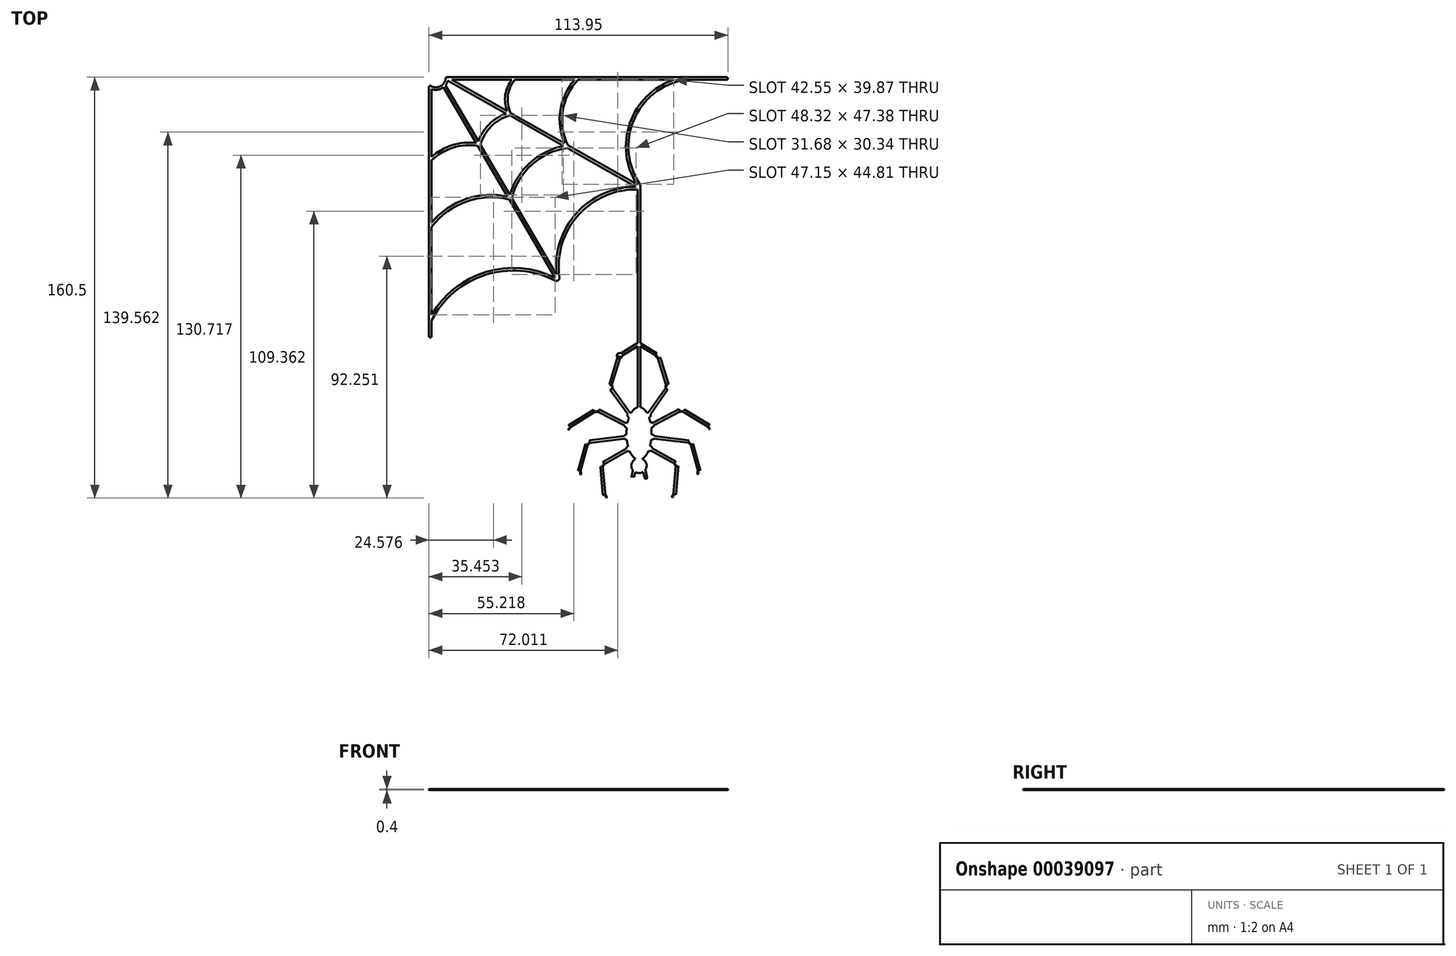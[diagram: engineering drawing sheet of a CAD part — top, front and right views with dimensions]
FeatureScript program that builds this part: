
annotation { "Feature Type Name" : "Feature", "Feature Type Description" : "" }
export const myFeature = defineFeature(function(context is Context, id is Id, definition is map)
    precondition{}
    {
        {
            var Q0;
            Q0=qCreatedBy(makeId("Top.planeOp"),FACE);
            var sketch = newSketch(context, id + "F0", { "sketchPlane" : qUnion([Q0])});
            skPoint(sketch, "E0.endSnap0", {"position": v(-98.37, 53.24) * mm});
            skLineSegment(sketch, "E1.5.startCap", {"start": v(-10.38, 79.69) * mm, "end": v(-10.38, 79.69) * mm});
            skArc(sketch, "E1.5.left", {"start": v(-10.2, 78.7) * mm, "mid": v(-29.48, 63.21) * mm, "end": v(-26.9, 38.61) * mm});
            skArc(sketch, "E1.5.right", {"start": v(-14.23, 78.7) * mm, "mid": v(-30.95, 62.17) * mm, "end": v(-28.25, 38.83) * mm});
            skArc(sketch, "E1.6.startCap", {"start": v(-101.16, 79.24) * mm, "mid": v(-101, 79.57) * mm, "end": v(-100.66, 79.7) * mm});
            skArc(sketch, "E1.6.endCap", {"start": v(5.93, 79.7) * mm, "mid": v(6.43, 79.2) * mm, "end": v(5.93, 78.7) * mm});
            skLineSegment(sketch, "E1.6.left", {"start": v(-100.66, 79.7) * mm, "end": v(5.93, 79.7) * mm});
            skArc(sketch, "E1.7.startCap", {"start": v(-101.16, 79.24) * mm, "mid": v(-101, 79.57) * mm, "end": v(-100.66, 79.7) * mm});
            skLineSegment(sketch, "E1.7.left", {"start": v(-98.76, 78.7) * mm, "end": v(-77.67, 66.77) * mm});
            skLineSegment(sketch, "E1.7.right", {"start": v(-100.3, 78.41) * mm, "end": v(-78.03, 65.83) * mm});
            skLineSegment(sketch, "E1.8.left", {"start": v(-101.22, 76.58) * mm, "end": v(-88.68, 55.2) * mm});
            skLineSegment(sketch, "E1.8.right", {"start": v(-101.96, 75.86) * mm, "end": v(-89.5, 54.6) * mm});
            skArc(sketch, "E1.9.startCap", {"start": v(-107.52, 75.91) * mm, "mid": v(-107.27, 76.35) * mm, "end": v(-106.77, 76.35) * mm});
            skArc(sketch, "E1.9.endCap", {"start": v(-106.52, -19.05) * mm, "mid": v(-107.02, -19.55) * mm, "end": v(-107.52, -19.05) * mm});
            skLineSegment(sketch, "E1.9.left", {"start": v(-106.52, 75.13) * mm, "end": v(-106.52, 49.32) * mm});
            skLineSegment(sketch, "E1.9.right", {"start": v(-107.52, 75.91) * mm, "end": v(-107.52, -19.05) * mm});
            skArc(sketch, "E1.10.startCap", {"start": v(-75.03, 79.7) * mm, "mid": v(-75.03, 79.7) * mm, "end": v(-75.02, 79.7) * mm});
            skArc(sketch, "E1.10.left", {"start": v(-74.65, 78.87) * mm, "mid": v(-77.4, 72.71) * mm, "end": v(-76.38, 66.04) * mm});
            skArc(sketch, "E1.15.startCap", {"start": v(-76.4, 33.94) * mm, "mid": v(-76.22, 33.86) * mm, "end": v(-76.1, 33.71) * mm});
            skArc(sketch, "E1.15.endCap", {"start": v(-107.52, 22.78) * mm, "mid": v(-107.5, 22.94) * mm, "end": v(-107.42, 23.08) * mm});
            skArc(sketch, "E1.15.left", {"start": v(-76.65, 32.97) * mm, "mid": v(-93.23, 32.29) * mm, "end": v(-106.62, 22.48) * mm});
            skArc(sketch, "E1.20.right", {"start": v(-28.61, 37.89) * mm, "mid": v(-51.23, 27.9) * mm, "end": v(-58.92, 4.4) * mm});
            skLineSegment(sketch, "E1.22.endCap", {"start": v(-106.57, -13.15) * mm, "end": v(-106.57, -13.15) * mm});
            skArc(sketch, "E1.22.left", {"start": v(-59.5, 2.14) * mm, "mid": v(-86.21, 4.27) * mm, "end": v(-106.57, -13.15) * mm});
            skArc(sketch, "E1.22.right", {"start": v(-59.37, 3.2) * mm, "mid": v(-85.75, 5.46) * mm, "end": v(-106.52, -10.96) * mm});
            skArc(sketch, "E1.23.startCap", {"start": v(-50.82, 79.7) * mm, "mid": v(-50.81, 79.7) * mm, "end": v(-50.8, 79.7) * mm});
            skArc(sketch, "E1.23.left", {"start": v(-50.46, 78.84) * mm, "mid": v(-56.52, 66.83) * mm, "end": v(-54.42, 53.53) * mm});
            skArc(sketch, "E1.23.right", {"start": v(-51.96, 78.7) * mm, "mid": v(-57.44, 67.14) * mm, "end": v(-55.86, 54.44) * mm});
            skArc(sketch, "E1.28.left", {"start": v(-76.53, 65.14) * mm, "mid": v(-83.77, 61) * mm, "end": v(-87.94, 53.76) * mm});
            skArc(sketch, "E1.31.left", {"start": v(-88.62, 53.46) * mm, "mid": v(-98.33, 52.83) * mm, "end": v(-106.67, 47.81) * mm});
            skArc(sketch, "E1.31.right", {"start": v(-89.5, 54.6) * mm, "mid": v(-98.58, 53.8) * mm, "end": v(-106.52, 49.32) * mm});
            skArc(sketch, "E1.36.startCap", {"start": v(-54.83, 53.74) * mm, "mid": v(-54.66, 53.73) * mm, "end": v(-54.5, 53.68) * mm});
            skLineSegment(sketch, "E1.36.endCap", {"start": v(-76.04, 33.34) * mm, "end": v(-76.04, 33.34) * mm});
            skArc(sketch, "E1.36.left", {"start": v(-54.81, 52.73) * mm, "mid": v(-68.39, 46.28) * mm, "end": v(-76.04, 33.34) * mm});
            skArc(sketch, "E1.36.right", {"start": v(-56.23, 53.5) * mm, "mid": v(-69.1, 47) * mm, "end": v(-76.7, 34.75) * mm});
            skArc(sketch, "E1.38.startCap", {"start": v(-107.52, 75.91) * mm, "mid": v(-107.27, 76.35) * mm, "end": v(-106.77, 76.35) * mm});
            skArc(sketch, "E1.38.endCap", {"start": v(-101.16, 79.24) * mm, "mid": v(-101, 79.57) * mm, "end": v(-100.66, 79.7) * mm});
            skArc(sketch, "E1.38.left", {"start": v(-106.77, 76.35) * mm, "mid": v(-103.17, 76.26) * mm, "end": v(-101.16, 79.24) * mm});
            skArc(sketch, "E1.38.right", {"start": v(-106.52, 75.13) * mm, "mid": v(-104.14, 74.9) * mm, "end": v(-101.96, 75.86) * mm});
            skLineSegment(sketch, "E2.trimOffspring", {"start": v(-106.52, -13.05) * mm, "end": v(-106.52, -19.05) * mm});
            skArc(sketch, "E3.trimOffspring", {"start": v(-107.52, -12.93) * mm, "mid": v(-107.5, -12.8) * mm, "end": v(-107.46, -12.7) * mm});
            skLineSegment(sketch, "E4.trimOffspring", {"start": v(-106.52, 22.62) * mm, "end": v(-106.52, -10.96) * mm});
            skLineSegment(sketch, "E5.trimOffspring", {"start": v(-76.1, 33.71) * mm, "end": v(-58.92, 4.4) * mm});
            skLineSegment(sketch, "E6.trimOffspring", {"start": v(-76.96, 33.2) * mm, "end": v(-59.37, 3.2) * mm});
            skArc(sketch, "E7.trimOffspring", {"start": v(-77.55, 34.22) * mm, "mid": v(-93.43, 33.27) * mm, "end": v(-106.52, 24.22) * mm});
            skLineSegment(sketch, "E8.trimOffspring", {"start": v(-106.52, 47.96) * mm, "end": v(-106.52, 24.22) * mm});
            skLineSegment(sketch, "E9.trimOffspring", {"start": v(-88.1, 54.2) * mm, "end": v(-76.7, 34.75) * mm});
            skLineSegment(sketch, "E10.trimOffspring", {"start": v(-88.85, 53.5) * mm, "end": v(-77.55, 34.22) * mm});
            skLineSegment(sketch, "E11.trimOffspring", {"start": v(-76.4, 66.06) * mm, "end": v(-55.86, 54.44) * mm});
            skArc(sketch, "E12.trimOffspring", {"start": v(-78.03, 65.83) * mm, "mid": v(-84.6, 61.75) * mm, "end": v(-88.68, 55.2) * mm});
            skLineSegment(sketch, "E13.trimOffspring", {"start": v(-76.72, 65.09) * mm, "end": v(-56.23, 53.5) * mm});
            skLineSegment(sketch, "E14.trimOffspring", {"start": v(-54.85, 52.72) * mm, "end": v(-28.61, 37.89) * mm});
            skLineSegment(sketch, "E15.trimOffspring", {"start": v(-54.49, 53.66) * mm, "end": v(-28.25, 38.83) * mm});
            skArc(sketch, "E16.trimOffspring", {"start": v(-55.11, 52.87) * mm, "mid": v(-55.23, 52.96) * mm, "end": v(-55.31, 53.08) * mm});
            skLineSegment(sketch, "E17.trimOffspring", {"start": v(-10.25, 78.7) * mm, "end": v(5.93, 78.7) * mm});
            skLineSegment(sketch, "E18.trimOffspring", {"start": v(-50.6, 78.7) * mm, "end": v(-14.23, 78.7) * mm});
            skLineSegment(sketch, "E19.trimOffspring", {"start": v(-74.8, 78.7) * mm, "end": v(-51.96, 78.7) * mm});
            skLineSegment(sketch, "E20.trimOffspring", {"start": v(-98.76, 78.7) * mm, "end": v(-75.94, 78.7) * mm});
            skArc(sketch, "E21.trimOffspring", {"start": v(-101.22, 76.58) * mm, "mid": v(-100.66, 77.45) * mm, "end": v(-100.3, 78.41) * mm});
            skArc(sketch, "E22", {"start": v(-75.94, 78.7) * mm, "mid": v(-78.42, 72.97) * mm, "end": v(-77.67, 66.77) * mm});
            skLineSegment(sketch, "E23.0.right", {"start": v(-22.6, -53.42) * mm, "end": v(-10.92, -47.39) * mm});
            skLineSegment(sketch, "E23.21.left", {"start": v(0.43, -53.66) * mm, "end": v(2.06, -65.33) * mm});
            skEllipse(sketch, "E24", {"center": v(-27.45, -68.45) * mm, "majorRadius": 2.83 * mm, "minorRadius": 2.91 * mm, "majorAxis": v(0, 1)});
            skEllipse(sketch, "E25", {"center": v(-27.45, -56.16) * mm, "majorRadius": 10.03 * mm, "minorRadius": 4.77 * mm, "majorAxis": v(0, 1)});
            skLineSegment(sketch, "E23.0.left", {"start": v(-23.06, -52.53) * mm, "end": v(-11.37, -46.5) * mm});
            skLineSegment(sketch, "E23.3.right", {"start": v(-34.63, -26.94) * mm, "end": v(-27.9, -22.81) * mm});
            skLineSegment(sketch, "E23.17.left", {"start": v(-3.76, -71.27) * mm, "end": v(-6.93, -83.23) * mm});
            skLineSegment(sketch, "E23.3.left", {"start": v(-35.15, -26.09) * mm, "end": v(-27.9, -21.64) * mm});
            skLineSegment(sketch, "E23.35.right", {"start": v(-23.62, -62.32) * mm, "end": v(-13.14, -68.15) * mm});
            skLineSegment(sketch, "E23.26.left", {"start": v(-43.43, -47.46) * mm, "end": v(-54.48, -54.32) * mm});
            skLineSegment(sketch, "E23.25.right", {"start": v(-23.53, -49.46) * mm, "end": v(-15.96, -38.67) * mm});
            skLineSegment(sketch, "E23.21.right", {"start": v(-0.56, -53.8) * mm, "end": v(1.07, -65.47) * mm});
            skLineSegment(sketch, "E23.13.left", {"start": v(-26.92, -11.26) * mm, "end": v(-26.9, -21.74) * mm});
            skLineSegment(sketch, "E23.17.right", {"start": v(-4.72, -71.01) * mm, "end": v(-7.9, -82.97) * mm});
            skLineSegment(sketch, "E23.25.left", {"start": v(-24.35, -48.88) * mm, "end": v(-16.78, -38.1) * mm});
            skLineSegment(sketch, "E23.8.endCap", {"start": v(-27.36, 17.93) * mm, "end": v(-27.36, 17.93) * mm});
            skLineSegment(sketch, "E23.34.right", {"start": v(-15.9, -38.24) * mm, "end": v(-19.6, -26.32) * mm});
            skLineSegment(sketch, "E23.12.left", {"start": v(-12.4, -67.75) * mm, "end": v(-13.36, -80.35) * mm});
            skLineSegment(sketch, "E23.16.right", {"start": v(-30.48, -48.9) * mm, "end": v(-38.12, -38.16) * mm});
            skLineSegment(sketch, "E23.34.left", {"start": v(-16.85, -38.53) * mm, "end": v(-20.55, -26.62) * mm});
            skLineSegment(sketch, "E23.16.left", {"start": v(-31.3, -49.48) * mm, "end": v(-38.93, -38.74) * mm});
            skLineSegment(sketch, "E23.29.right", {"start": v(-55.24, -53.82) * mm, "end": v(-56.8, -65.5) * mm});
            skLineSegment(sketch, "E23.29.left", {"start": v(-54.25, -53.96) * mm, "end": v(-55.8, -65.63) * mm});
            skLineSegment(sketch, "E23.24.right", {"start": v(-41.1, -80.82) * mm, "end": v(-32.4, -90.55) * mm});
            skLineSegment(sketch, "E23.11.right", {"start": v(-38.05, -38.6) * mm, "end": v(-34.41, -26.66) * mm});
            skLineSegment(sketch, "E23.19.right", {"start": v(-42.27, -67.95) * mm, "end": v(-41.23, -80.53) * mm});
            skLineSegment(sketch, "E23.33.right", {"start": v(-11.4, -47.37) * mm, "end": v(-0.32, -54.16) * mm});
            skLineSegment(sketch, "E23.24.left", {"start": v(-40.24, -80.28) * mm, "end": v(-31.66, -89.89) * mm});
            skLineSegment(sketch, "E23.11.left", {"start": v(-39, -38.3) * mm, "end": v(-35.37, -26.37) * mm});
            skLineSegment(sketch, "E23.37.right", {"start": v(-47.7, -59.34) * mm, "end": v(-50.94, -71.15) * mm});
            skLineSegment(sketch, "E23.1.right", {"start": v(-19.81, -26.04) * mm, "end": v(-26.9, -21.74) * mm});
            skLineSegment(sketch, "E23.19.left", {"start": v(-41.27, -67.86) * mm, "end": v(-40.24, -80.28) * mm});
            skLineSegment(sketch, "E23.33.left", {"start": v(-10.88, -46.51) * mm, "end": v(0.2, -53.3) * mm});
            skLineSegment(sketch, "E23.30.right", {"start": v(-22.67, -58.03) * mm, "end": v(-7.61, -59.85) * mm});
            skLineSegment(sketch, "E23.37.left", {"start": v(-46.73, -59.6) * mm, "end": v(-49.98, -71.4) * mm});
            skLineSegment(sketch, "E23.27.right", {"start": v(-50.94, -71.4) * mm, "end": v(-47.7, -83.35) * mm});
            skLineSegment(sketch, "E23.1.left", {"start": v(-20.33, -26.9) * mm, "end": v(-26.9, -22.91) * mm});
            skLineSegment(sketch, "E23.14.right", {"start": v(-32.24, -57.07) * mm, "end": v(-47.28, -58.97) * mm});
            skLineSegment(sketch, "E23.27.left", {"start": v(-49.98, -71.15) * mm, "end": v(-46.73, -83.08) * mm});
            skLineSegment(sketch, "E23.32.right", {"start": v(-14.35, -80.1) * mm, "end": v(-22.87, -89.76) * mm});
            skLineSegment(sketch, "E23.14.left", {"start": v(-32.11, -58.06) * mm, "end": v(-47.15, -59.97) * mm});
            skLineSegment(sketch, "E23.18.right", {"start": v(-31.75, -52.56) * mm, "end": v(-43.47, -46.6) * mm});
            skLineSegment(sketch, "E23.32.left", {"start": v(-13.49, -80.64) * mm, "end": v(-22.12, -90.42) * mm});
            skLineSegment(sketch, "E23.18.left", {"start": v(-32.2, -53.45) * mm, "end": v(-43.93, -47.48) * mm});
            skLineSegment(sketch, "E23.4.right", {"start": v(-8.04, -59.49) * mm, "end": v(-4.72, -71.28) * mm});
            skLineSegment(sketch, "E23.4.left", {"start": v(-7.07, -59.22) * mm, "end": v(-3.76, -71) * mm});
            skLineSegment(sketch, "E23.12.right", {"start": v(-13.4, -67.68) * mm, "end": v(-14.35, -80.1) * mm});
            skLineSegment(sketch, "E23.26.right", {"start": v(-43.96, -46.61) * mm, "end": v(-55, -53.47) * mm});
            skCircle(sketch, "E26", {"center": v(-31.33, -62.01) * mm, "radius": 1 * mm});
            skArc(sketch, "E23.0.startCap", {"start": v(-22.6, -53.42) * mm, "mid": v(-22.72, -53.47) * mm, "end": v(-22.86, -53.48) * mm});
            skArc(sketch, "E23.21.endCap", {"start": v(2.06, -65.33) * mm, "mid": v(1.63, -65.9) * mm, "end": v(1.07, -65.47) * mm});
            skCircle(sketch, "E27", {"center": v(-22.83, -52.98) * mm, "radius": 1 * mm});
            skArc(sketch, "E23.39.startCap", {"start": v(-29.8, -70.51) * mm, "mid": v(-29.2, -70.14) * mm, "end": v(-28.83, -70.75) * mm});
            skArc(sketch, "E23.42.endCap", {"start": v(-25.3, -74.86) * mm, "mid": v(-25.98, -75.06) * mm, "end": v(-26.17, -74.38) * mm});
            skArc(sketch, "E23.29.endCap", {"start": v(-55.8, -65.63) * mm, "mid": v(-56.37, -66.06) * mm, "end": v(-56.8, -65.5) * mm});
            skArc(sketch, "E23.24.endCap", {"start": v(-31.66, -89.89) * mm, "mid": v(-31.7, -90.6) * mm, "end": v(-32.4, -90.55) * mm});
            skArc(sketch, "E23.17.endCap", {"start": v(-6.93, -83.23) * mm, "mid": v(-7.54, -83.58) * mm, "end": v(-7.9, -82.97) * mm});
            skArc(sketch, "E23.41.startCap", {"start": v(-25.88, -70.74) * mm, "mid": v(-25.52, -70.13) * mm, "end": v(-24.9, -70.5) * mm});
            skArc(sketch, "E23.27.endCap", {"start": v(-46.73, -83.08) * mm, "mid": v(-47.09, -83.7) * mm, "end": v(-47.7, -83.35) * mm});
            skArc(sketch, "E23.32.endCap", {"start": v(-22.12, -90.42) * mm, "mid": v(-22.83, -90.46) * mm, "end": v(-22.87, -89.76) * mm});
            skArc(sketch, "E23.14.startCap", {"start": v(-32.24, -57.07) * mm, "mid": v(-32.22, -57.06) * mm, "end": v(-32.2, -57.06) * mm});
            skCircle(sketch, "E28", {"center": v(-32.18, -57.56) * mm, "radius": 1 * mm});
            skArc(sketch, "E23.40.endCap", {"start": v(-28.51, -74.38) * mm, "mid": v(-28.7, -75.07) * mm, "end": v(-29.39, -74.88) * mm});
            skArc(sketch, "E23.13.endCap", {"start": v(-26.88, -58.8) * mm, "mid": v(-27.38, -59.3) * mm, "end": v(-27.88, -58.8) * mm});
            skArc(sketch, "E23.25.endCap", {"start": v(-15.9, -38.24) * mm, "mid": v(-15.88, -38.46) * mm, "end": v(-15.96, -38.67) * mm});
            skArc(sketch, "E23.25.startCap", {"start": v(-23.53, -49.46) * mm, "mid": v(-23.66, -49.58) * mm, "end": v(-23.82, -49.66) * mm});
            skArc(sketch, "E23.16.endCap", {"start": v(-38.93, -38.74) * mm, "mid": v(-39.02, -38.53) * mm, "end": v(-39, -38.3) * mm});
            skCircle(sketch, "E29", {"center": v(-31.98, -53) * mm, "radius": 1 * mm});
            skCircle(sketch, "E30", {"center": v(-23.37, -61.89) * mm, "radius": 1 * mm});
            skCircle(sketch, "E31", {"center": v(-38.52, -38.45) * mm, "radius": 1 * mm});
            skArc(sketch, "E23.18.startCap", {"start": v(-32.05, -53.5) * mm, "mid": v(-32.13, -53.48) * mm, "end": v(-32.2, -53.45) * mm});
            skCircle(sketch, "E32", {"center": v(-23.94, -49.17) * mm, "radius": 1 * mm});
            skCircle(sketch, "E33", {"center": v(-16.37, -38.39) * mm, "radius": 1 * mm});
            skCircle(sketch, "E34", {"center": v(-30.89, -49.2) * mm, "radius": 1 * mm});
            skArc(sketch, "E23.30.startCap", {"start": v(-22.67, -58.03) * mm, "mid": v(-22.72, -58.02) * mm, "end": v(-22.77, -58) * mm});
            skArc(sketch, "E23.12.endCap", {"start": v(-13.36, -80.35) * mm, "mid": v(-13.4, -80.5) * mm, "end": v(-13.49, -80.64) * mm});
            skArc(sketch, "E23.34.startCap", {"start": v(-15.9, -38.24) * mm, "mid": v(-15.88, -38.46) * mm, "end": v(-15.96, -38.67) * mm});
            skArc(sketch, "E23.16.startCap", {"start": v(-31.08, -49.65) * mm, "mid": v(-31.2, -49.58) * mm, "end": v(-31.3, -49.48) * mm});
            skCircle(sketch, "E35", {"center": v(-54.74, -53.9) * mm, "radius": 1 * mm});
            skArc(sketch, "E23.11.startCap", {"start": v(-38.93, -38.74) * mm, "mid": v(-39.02, -38.53) * mm, "end": v(-39, -38.3) * mm});
            skArc(sketch, "E23.19.endCap", {"start": v(-41.1, -80.82) * mm, "mid": v(-41.19, -80.69) * mm, "end": v(-41.23, -80.53) * mm});
            skCircle(sketch, "E36", {"center": v(-47.22, -59.47) * mm, "radius": 1 * mm});
            skArc(sketch, "E23.37.startCap", {"start": v(-47.7, -59.34) * mm, "mid": v(-47.54, -59.1) * mm, "end": v(-47.28, -58.97) * mm});
            skCircle(sketch, "E37", {"center": v(-40.73, -80.49) * mm, "radius": 1 * mm});
            skCircle(sketch, "E38", {"center": v(-22.6, -57.53) * mm, "radius": 1 * mm});
            skArc(sketch, "E23.35.startCap", {"start": v(-23.62, -62.32) * mm, "mid": v(-23.65, -62.3) * mm, "end": v(-23.68, -62.28) * mm});
            skCircle(sketch, "E39", {"center": v(-13.86, -80.3) * mm, "radius": 1 * mm});
            skLineSegment(sketch, "E23.39.right", {"start": v(-29.8, -70.51) * mm, "end": v(-30.37, -72.86) * mm});
            skArc(sketch, "E23.0.endCap", {"start": v(-11.37, -46.5) * mm, "mid": v(-11.13, -46.44) * mm, "end": v(-10.88, -46.51) * mm});
            skCircle(sketch, "E40", {"center": v(-50.46, -71.28) * mm, "radius": 1 * mm});
            skArc(sketch, "E23.40.startCap", {"start": v(-30.32, -73.22) * mm, "mid": v(-30.13, -72.54) * mm, "end": v(-29.45, -72.73) * mm});
            skCircle(sketch, "E41", {"center": v(-12.9, -67.72) * mm, "radius": 1 * mm});
            skLineSegment(sketch, "E23.42.right", {"start": v(-25.25, -72.72) * mm, "end": v(-26.17, -74.38) * mm});
            skCircle(sketch, "E42", {"center": v(-4.24, -71.14) * mm, "radius": 1 * mm});
            skLineSegment(sketch, "E23.42.left", {"start": v(-24.37, -73.2) * mm, "end": v(-25.3, -74.86) * mm});
            skArc(sketch, "E23.12.startCap", {"start": v(-12.65, -67.28) * mm, "mid": v(-12.46, -67.48) * mm, "end": v(-12.4, -67.75) * mm});
            skCircle(sketch, "E43", {"center": v(-0.06, -53.73) * mm, "radius": 1 * mm});
            skArc(sketch, "E23.42.startCap", {"start": v(-25.25, -72.72) * mm, "mid": v(-24.57, -72.52) * mm, "end": v(-24.37, -73.2) * mm});
            skCircle(sketch, "E44", {"center": v(-11.15, -46.94) * mm, "radius": 1 * mm});
            skLineSegment(sketch, "E23.41.right", {"start": v(-25.88, -70.74) * mm, "end": v(-25.3, -73.08) * mm});
            skArc(sketch, "E23.29.startCap", {"start": v(-55.24, -53.82) * mm, "mid": v(-55.16, -53.62) * mm, "end": v(-55, -53.47) * mm});
            skCircle(sketch, "E45", {"center": v(-43.7, -47.04) * mm, "radius": 1 * mm});
            skArc(sketch, "E23.33.endCap", {"start": v(0.2, -53.3) * mm, "mid": v(0.36, -53.46) * mm, "end": v(0.43, -53.66) * mm});
            skLineSegment(sketch, "E23.41.left", {"start": v(-24.9, -70.5) * mm, "end": v(-24.32, -72.84) * mm});
            skArc(sketch, "E23.24.startCap", {"start": v(-41.1, -80.82) * mm, "mid": v(-41.19, -80.69) * mm, "end": v(-41.23, -80.53) * mm});
            skArc(sketch, "E23.37.endCap", {"start": v(-50.94, -71.4) * mm, "mid": v(-50.96, -71.28) * mm, "end": v(-50.94, -71.15) * mm});
            skLineSegment(sketch, "E23.40.right", {"start": v(-30.32, -73.22) * mm, "end": v(-29.39, -74.88) * mm});
            skArc(sketch, "E23.14.endCap", {"start": v(-47.7, -59.34) * mm, "mid": v(-47.54, -59.1) * mm, "end": v(-47.28, -58.97) * mm});
            skLineSegment(sketch, "E23.39.left", {"start": v(-28.83, -70.75) * mm, "end": v(-29.4, -73.1) * mm});
            skLineSegment(sketch, "E23.40.left", {"start": v(-29.45, -72.73) * mm, "end": v(-28.51, -74.38) * mm});
            skArc(sketch, "E23.18.endCap", {"start": v(-43.96, -46.61) * mm, "mid": v(-43.72, -46.54) * mm, "end": v(-43.47, -46.6) * mm});
            skArc(sketch, "E23.32.startCap", {"start": v(-13.36, -80.35) * mm, "mid": v(-13.4, -80.5) * mm, "end": v(-13.49, -80.64) * mm});
            skArc(sketch, "E23.26.endCap", {"start": v(-55.24, -53.82) * mm, "mid": v(-55.16, -53.62) * mm, "end": v(-55, -53.47) * mm});
            skArc(sketch, "E23.39.endCap", {"start": v(-29.4, -73.1) * mm, "mid": v(-30, -73.46) * mm, "end": v(-30.37, -72.86) * mm});
            skArc(sketch, "E23.26.startCap", {"start": v(-43.96, -46.61) * mm, "mid": v(-43.72, -46.54) * mm, "end": v(-43.47, -46.6) * mm});
            skArc(sketch, "E23.41.endCap", {"start": v(-24.32, -72.84) * mm, "mid": v(-24.69, -73.45) * mm, "end": v(-25.3, -73.08) * mm});
            skArc(sketch, "E23.33.startCap", {"start": v(-11.37, -46.5) * mm, "mid": v(-11.13, -46.44) * mm, "end": v(-10.88, -46.51) * mm});
            skArc(sketch, "E23.35.endCap", {"start": v(-12.65, -67.28) * mm, "mid": v(-12.46, -67.48) * mm, "end": v(-12.4, -67.75) * mm});
            skArc(sketch, "E23.21.startCap", {"start": v(0.2, -53.3) * mm, "mid": v(0.36, -53.46) * mm, "end": v(0.43, -53.66) * mm});
            skArc(sketch, "E23.27.startCap", {"start": v(-50.94, -71.4) * mm, "mid": v(-50.96, -71.28) * mm, "end": v(-50.94, -71.15) * mm});
            skArc(sketch, "E23.4.endCap", {"start": v(-3.76, -71) * mm, "mid": v(-3.74, -71.14) * mm, "end": v(-3.76, -71.27) * mm});
            skArc(sketch, "E23.3.startCap", {"start": v(-34.63, -26.94) * mm, "mid": v(-35.32, -26.78) * mm, "end": v(-35.15, -26.09) * mm});
            skArc(sketch, "E23.17.startCap", {"start": v(-3.76, -71) * mm, "mid": v(-3.74, -71.14) * mm, "end": v(-3.76, -71.27) * mm});
            skCircle(sketch, "E46", {"center": v(-34.9, -26.51) * mm, "radius": 1 * mm});
            skArc(sketch, "E23.1.startCap", {"start": v(-19.81, -26.04) * mm, "mid": v(-19.68, -26.16) * mm, "end": v(-19.6, -26.32) * mm});
            skCircle(sketch, "E47", {"center": v(-20.07, -26.47) * mm, "radius": 1 * mm});
            skArc(sketch, "E23.30.endCap", {"start": v(-7.5, -58.86) * mm, "mid": v(-7.23, -58.97) * mm, "end": v(-7.07, -59.22) * mm});
            skCircle(sketch, "E48", {"center": v(-7.55, -59.35) * mm, "radius": 1 * mm});
            skArc(sketch, "E23.11.endCap", {"start": v(-35.37, -26.37) * mm, "mid": v(-35.29, -26.2) * mm, "end": v(-35.15, -26.09) * mm});
            skArc(sketch, "E23.2.endCap", {"start": v(-42.27, -67.95) * mm, "mid": v(-42.2, -67.67) * mm, "end": v(-42.01, -67.47) * mm});
            skCircle(sketch, "E49", {"center": v(-41.77, -67.9) * mm, "radius": 1 * mm});
            skArc(sketch, "E23.34.endCap", {"start": v(-19.81, -26.04) * mm, "mid": v(-19.68, -26.16) * mm, "end": v(-19.6, -26.32) * mm});
            skArc(sketch, "E23.4.startCap", {"start": v(-7.5, -58.86) * mm, "mid": v(-7.23, -58.97) * mm, "end": v(-7.07, -59.22) * mm});
            skArc(sketch, "E23.19.startCap", {"start": v(-42.27, -67.95) * mm, "mid": v(-42.2, -67.67) * mm, "end": v(-42.01, -67.47) * mm});
            skLineSegment(sketch, "E50.trimOffspring", {"start": v(-27.95, 36.88) * mm, "end": v(-27.9, -21.64) * mm});
            skArc(sketch, "E51.trimOffspring", {"start": v(-27.95, 36.88) * mm, "mid": v(-50.65, 27.05) * mm, "end": v(-57.78, 3.36) * mm});
            skLineSegment(sketch, "E52.trimOffspring", {"start": v(-27.9, -22.81) * mm, "end": v(-27.88, -58.8) * mm});
            skLineSegment(sketch, "E53.trimOffspring", {"start": v(-26.9, -22.91) * mm, "end": v(-26.88, -58.8) * mm});
            skArc(sketch, "E54", {"start": v(-59.5, 2.14) * mm, "mid": v(-58.26, 2.23) * mm, "end": v(-57.78, 3.36) * mm});
            skLineSegment(sketch, "E55", {"start": v(-26.92, -11.26) * mm, "end": v(-26.9, 38.61) * mm});
            skLineSegment(sketch, "E56.trimOffspring", {"start": v(-22.7, -57.02) * mm, "end": v(-7.5, -58.86) * mm});
            skLineSegment(sketch, "E57.trimOffspring", {"start": v(-23.37, -61.32) * mm, "end": v(-12.65, -67.28) * mm});
            skLineSegment(sketch, "E58.trimOffspring", {"start": v(-31.48, -61.53) * mm, "end": v(-42.01, -67.47) * mm});
            skLineSegment(sketch, "E59.trimOffspring", {"start": v(-31.15, -62.5) * mm, "end": v(-41.52, -68.34) * mm});
            skSolve(sketch);
        }
        {
            var Q0;
            {var subQ3=sQuery(id+"F0.wireOp",EDGE,"E23.26.left");var subQ5=sQuery(id+"F0.wireOp",EDGE,"E45");var subQ7=makeQuery(id+"F0.imprint","INTERSECT",VERTEX,{"derivedFrom":[subQ3,subQ5]});Q0=makeQuery(id+"F0.imprint","IMPRINT",FACE,{"disambiguationData":[TD([[makeQuery(id+"F0.imprint","IMPRINT",EDGE,{"disambiguationData":[TD([[subQ7,-1.0]])],"derivedFrom":subQ3}),-1.0]])]});}
            var Q1;
            {var subQ0=sQuery(id+"F0.wireOp",EDGE,"E49");var subQ3=sQuery(id+"F0.wireOp",EDGE,"E23.19.right");var subQ4=makeQuery(id+"F0.imprint","INTERSECT",VERTEX,{"derivedFrom":[subQ3,subQ0]});Q1=makeQuery(id+"F0.imprint","IMPRINT",FACE,{"disambiguationData":[TD([[makeQuery(id+"F0.imprint","IMPRINT",EDGE,{"disambiguationData":[TD([[subQ4,-1.0]])],"derivedFrom":subQ3}),1.0]])]});}
            var Q2;
            {var subQ3=sQuery(id+"F0.wireOp",EDGE,"E23.0.right");var subQ5=sQuery(id+"F0.wireOp",EDGE,"E27");var subQ7=makeQuery(id+"F0.imprint","INTERSECT",VERTEX,{"derivedFrom":[subQ3,subQ5]});Q2=makeQuery(id+"F0.imprint","IMPRINT",FACE,{"disambiguationData":[TD([[makeQuery(id+"F0.imprint","IMPRINT",EDGE,{"disambiguationData":[TD([[subQ7,-1.0]])],"derivedFrom":subQ3}),1.0]])]});}
            var Q3;
            {var subQ0=sQuery(id+"F0.wireOp",EDGE,"E23.21.endCap");Q3=makeQuery(id+"F0.imprint","IMPRINT",FACE,{"disambiguationData":[TD([[makeQuery(id+"F0.imprint","IMPRINT",EDGE,{"derivedFrom":subQ0}),-1.0]])]});}
            var Q4;
            {var subQ0=sQuery(id+"F0.wireOp",EDGE,"E41");var subQ3=sQuery(id+"F0.wireOp",EDGE,"E23.12.left");var subQ4=makeQuery(id+"F0.imprint","INTERSECT",VERTEX,{"derivedFrom":[subQ3,subQ0]});Q4=makeQuery(id+"F0.imprint","IMPRINT",FACE,{"disambiguationData":[TD([[makeQuery(id+"F0.imprint","IMPRINT",EDGE,{"disambiguationData":[TD([[subQ4,-1.0]])],"derivedFrom":subQ3}),-1.0]])]});}
            var Q5;
            {var subQ0=sQuery(id+"F0.wireOp",EDGE,"E23.39.left");var subQ1=sQuery(id+"F0.wireOp",EDGE,"E24");var subQ2=makeQuery(id+"F0.imprint","INTERSECT",VERTEX,{"derivedFrom":[subQ1,subQ0]});Q5=makeQuery(id+"F0.imprint","IMPRINT",FACE,{"disambiguationData":[TD([[makeQuery(id+"F0.imprint","IMPRINT",EDGE,{"disambiguationData":[TD([[subQ2,-1.0]])],"derivedFrom":subQ1}),1.0]])]});}
            var Q6;
            {var subQ5=sQuery(id+"F0.wireOp",EDGE,"E23.17.endCap");Q6=makeQuery(id+"F0.imprint","IMPRINT",FACE,{"disambiguationData":[TD([[makeQuery(id+"F0.imprint","IMPRINT",EDGE,{"derivedFrom":subQ5}),-1.0]])]});}
            var Q7;
            {var subQ3=sQuery(id+"F0.wireOp",EDGE,"E23.25.right");var subQ5=sQuery(id+"F0.wireOp",EDGE,"E32");var subQ7=makeQuery(id+"F0.imprint","INTERSECT",VERTEX,{"derivedFrom":[subQ3,subQ5]});Q7=makeQuery(id+"F0.imprint","IMPRINT",FACE,{"disambiguationData":[TD([[makeQuery(id+"F0.imprint","IMPRINT",EDGE,{"disambiguationData":[TD([[subQ7,-1.0]])],"derivedFrom":subQ3}),1.0]])]});}
            var Q8;
            {var subQ0=sQuery(id+"F0.wireOp",EDGE,"E33");var subQ3=sQuery(id+"F0.wireOp",EDGE,"E23.34.right");var subQ4=makeQuery(id+"F0.imprint","INTERSECT",VERTEX,{"derivedFrom":[subQ3,subQ0]});Q8=makeQuery(id+"F0.imprint","IMPRINT",FACE,{"disambiguationData":[TD([[makeQuery(id+"F0.imprint","IMPRINT",EDGE,{"disambiguationData":[TD([[subQ4,-1.0]])],"derivedFrom":subQ3}),1.0]])]});}
            var Q9;
            {var subQ3=sQuery(id+"F0.wireOp",EDGE,"E23.13.endCap");Q9=makeQuery(id+"F0.imprint","IMPRINT",FACE,{"disambiguationData":[TD([[makeQuery(id+"F0.imprint","IMPRINT",EDGE,{"derivedFrom":subQ3}),1.0]])]});}
            var Q10;
            {var subQ0=sQuery(id+"F0.wireOp",EDGE,"E31");var subQ1=sQuery(id+"F0.wireOp",EDGE,"E23.11.right");var subQ2=makeQuery(id+"F0.imprint","INTERSECT",VERTEX,{"derivedFrom":[subQ1,subQ0]});Q10=makeQuery(id+"F0.imprint","IMPRINT",FACE,{"disambiguationData":[TD([[makeQuery(id+"F0.imprint","IMPRINT",EDGE,{"disambiguationData":[TD([[subQ2,-1.0]])],"derivedFrom":subQ1}),1.0]])]});}
            var Q11;
            {var subQ3=sQuery(id+"F0.wireOp",EDGE,"E23.14.right");var subQ5=sQuery(id+"F0.wireOp",EDGE,"E28");var subQ7=makeQuery(id+"F0.imprint","INTERSECT",VERTEX,{"derivedFrom":[subQ3,subQ5]});Q11=makeQuery(id+"F0.imprint","IMPRINT",FACE,{"disambiguationData":[TD([[makeQuery(id+"F0.imprint","IMPRINT",EDGE,{"disambiguationData":[TD([[subQ7,-1.0]])],"derivedFrom":subQ3}),1.0]])]});}
            var Q12;
            {var subQ0=sQuery(id+"F0.wireOp",EDGE,"E23.24.endCap");Q12=makeQuery(id+"F0.imprint","IMPRINT",FACE,{"disambiguationData":[TD([[makeQuery(id+"F0.imprint","IMPRINT",EDGE,{"derivedFrom":subQ0}),-1.0]])]});}
            var Q13;
            {var subQ3=sQuery(id+"F0.wireOp",EDGE,"E23.18.right");var subQ5=sQuery(id+"F0.wireOp",EDGE,"E29");var subQ7=makeQuery(id+"F0.imprint","INTERSECT",VERTEX,{"derivedFrom":[subQ3,subQ5]});Q13=makeQuery(id+"F0.imprint","IMPRINT",FACE,{"disambiguationData":[TD([[makeQuery(id+"F0.imprint","IMPRINT",EDGE,{"disambiguationData":[TD([[subQ7,-1.0]])],"derivedFrom":subQ3}),1.0]])]});}
            var Q14;
            {var subQ0=sQuery(id+"F0.wireOp",EDGE,"E25");var subQ1=sQuery(id+"F0.wireOp",EDGE,"E24");var subQ3=makeQuery(id+"F0.imprint","INTERSECT",VERTEX,{"disambiguationData":[OD(0.0)],"derivedFrom":[subQ1,subQ0]});Q14=makeQuery(id+"F0.imprint","IMPRINT",FACE,{"disambiguationData":[TD([[makeQuery(id+"F0.imprint","IMPRINT",EDGE,{"disambiguationData":[TD([[subQ3,-1.0]])],"derivedFrom":subQ1}),1.0]])]});}
            var Q15;
            {var subQ0=sQuery(id+"F0.wireOp",EDGE,"E23.27.endCap");Q15=makeQuery(id+"F0.imprint","IMPRINT",FACE,{"disambiguationData":[TD([[makeQuery(id+"F0.imprint","IMPRINT",EDGE,{"derivedFrom":subQ0}),-1.0]])]});}
            var Q16;
            {var subQ3=sQuery(id+"F0.wireOp",EDGE,"E23.30.right");var subQ5=sQuery(id+"F0.wireOp",EDGE,"E38");var subQ7=makeQuery(id+"F0.imprint","INTERSECT",VERTEX,{"derivedFrom":[subQ3,subQ5]});Q16=makeQuery(id+"F0.imprint","IMPRINT",FACE,{"disambiguationData":[TD([[makeQuery(id+"F0.imprint","IMPRINT",EDGE,{"disambiguationData":[TD([[subQ7,-1.0]])],"derivedFrom":subQ3}),1.0]])]});}
            var Q17;
            {var subQ3=sQuery(id+"F0.wireOp",EDGE,"E23.35.right");var subQ5=sQuery(id+"F0.wireOp",EDGE,"E30");var subQ7=makeQuery(id+"F0.imprint","INTERSECT",VERTEX,{"derivedFrom":[subQ3,subQ5]});Q17=makeQuery(id+"F0.imprint","IMPRINT",FACE,{"disambiguationData":[TD([[makeQuery(id+"F0.imprint","IMPRINT",EDGE,{"disambiguationData":[TD([[subQ7,-1.0]])],"derivedFrom":subQ3}),1.0]])]});}
            var Q18;
            {var subQ3=sQuery(id+"F0.wireOp",EDGE,"E26");var subQ5=sQuery(id+"F0.wireOp",EDGE,"E58.trimOffspring");var subQ7=makeQuery(id+"F0.imprint","INTERSECT",VERTEX,{"derivedFrom":[subQ3,subQ5]});Q18=makeQuery(id+"F0.imprint","IMPRINT",FACE,{"disambiguationData":[TD([[makeQuery(id+"F0.imprint","IMPRINT",EDGE,{"disambiguationData":[TD([[subQ7,-1.0]])],"derivedFrom":subQ3}),-1.0]])]});}
            var Q19;
            {var subQ0=sQuery(id+"F0.wireOp",EDGE,"E48");var subQ3=sQuery(id+"F0.wireOp",EDGE,"E23.4.right");var subQ4=makeQuery(id+"F0.imprint","INTERSECT",VERTEX,{"derivedFrom":[subQ3,subQ0]});Q19=makeQuery(id+"F0.imprint","IMPRINT",FACE,{"disambiguationData":[TD([[makeQuery(id+"F0.imprint","IMPRINT",EDGE,{"disambiguationData":[TD([[subQ4,-1.0]])],"derivedFrom":subQ3}),1.0]])]});}
            var Q20;
            {var subQ3=sQuery(id+"F0.wireOp",EDGE,"E23.13.endCap");Q20=makeQuery(id+"F0.imprint","IMPRINT",FACE,{"disambiguationData":[TD([[makeQuery(id+"F0.imprint","IMPRINT",EDGE,{"derivedFrom":subQ3}),-1.0]])]});}
            var Q21;
            {var subQ5=sQuery(id+"F0.wireOp",EDGE,"E23.32.endCap");Q21=makeQuery(id+"F0.imprint","IMPRINT",FACE,{"disambiguationData":[TD([[makeQuery(id+"F0.imprint","IMPRINT",EDGE,{"derivedFrom":subQ5}),-1.0]])]});}
            var Q22;
            {var subQ0=sQuery(id+"F0.wireOp",EDGE,"E34");var subQ1=sQuery(id+"F0.wireOp",EDGE,"E23.16.right");var subQ2=makeQuery(id+"F0.imprint","INTERSECT",VERTEX,{"derivedFrom":[subQ1,subQ0]});Q22=makeQuery(id+"F0.imprint","IMPRINT",FACE,{"disambiguationData":[TD([[makeQuery(id+"F0.imprint","IMPRINT",EDGE,{"disambiguationData":[TD([[subQ2,-1.0]])],"derivedFrom":subQ1}),1.0]])]});}
            var Q23;
            {var subQ3=sQuery(id+"F0.wireOp",EDGE,"E23.37.right");var subQ5=sQuery(id+"F0.wireOp",EDGE,"E36");var subQ7=makeQuery(id+"F0.imprint","INTERSECT",VERTEX,{"derivedFrom":[subQ3,subQ5]});Q23=makeQuery(id+"F0.imprint","IMPRINT",FACE,{"disambiguationData":[TD([[makeQuery(id+"F0.imprint","IMPRINT",EDGE,{"disambiguationData":[TD([[subQ7,-1.0]])],"derivedFrom":subQ3}),1.0]])]});}
            var Q24;
            {var subQ5=sQuery(id+"F0.wireOp",EDGE,"E23.29.endCap");Q24=makeQuery(id+"F0.imprint","IMPRINT",FACE,{"disambiguationData":[TD([[makeQuery(id+"F0.imprint","IMPRINT",EDGE,{"derivedFrom":subQ5}),-1.0]])]});}
            var Q25;
            {var subQ3=sQuery(id+"F0.wireOp",EDGE,"E23.33.right");var subQ5=sQuery(id+"F0.wireOp",EDGE,"E44");var subQ7=makeQuery(id+"F0.imprint","INTERSECT",VERTEX,{"derivedFrom":[subQ3,subQ5]});Q25=makeQuery(id+"F0.imprint","IMPRINT",FACE,{"disambiguationData":[TD([[makeQuery(id+"F0.imprint","IMPRINT",EDGE,{"disambiguationData":[TD([[subQ7,-1.0]])],"derivedFrom":subQ3}),1.0]])]});}
            var Q26;
            {var subQ1=sQuery(id+"F0.wireOp",EDGE,"E25");var subQ5=makeQuery(id+"F0.imprint","INTERSECT",VERTEX,{"derivedFrom":[subQ1,sQuery(id+"F0.wireOp",EDGE,"E58.trimOffspring")]});Q26=makeQuery(id+"F0.imprint","IMPRINT",FACE,{"disambiguationData":[TD([[makeQuery(id+"F0.imprint","IMPRINT",EDGE,{"disambiguationData":[TD([[subQ5,1.0]])],"derivedFrom":subQ1}),1.0]])]});}
            var Q27;
            {var subQ0=sQuery(id+"F0.wireOp",EDGE,"E59.trimOffspring");var subQ3=sQuery(id+"F0.wireOp",EDGE,"E25");var subQ4=makeQuery(id+"F0.imprint","INTERSECT",VERTEX,{"derivedFrom":[subQ3,subQ0]});Q27=makeQuery(id+"F0.imprint","IMPRINT",FACE,{"disambiguationData":[TD([[makeQuery(id+"F0.imprint","IMPRINT",EDGE,{"disambiguationData":[TD([[subQ4,-1.0]])],"derivedFrom":subQ3}),-1.0]])]});}
            var Q28;
            {var subQ3=sQuery(id+"F0.wireOp",EDGE,"E25");var subQ5=sQuery(id+"F0.wireOp",EDGE,"E58.trimOffspring");var subQ7=makeQuery(id+"F0.imprint","INTERSECT",VERTEX,{"derivedFrom":[subQ3,subQ5]});Q28=makeQuery(id+"F0.imprint","IMPRINT",FACE,{"disambiguationData":[TD([[makeQuery(id+"F0.imprint","IMPRINT",EDGE,{"disambiguationData":[TD([[subQ7,-1.0]])],"derivedFrom":subQ3}),-1.0]])]});}
            var Q29;
            {var subQ0=sQuery(id+"F0.wireOp",EDGE,"E56.trimOffspring");var subQ3=sQuery(id+"F0.wireOp",EDGE,"E25");var subQ4=makeQuery(id+"F0.imprint","INTERSECT",VERTEX,{"derivedFrom":[subQ3,subQ0]});Q29=makeQuery(id+"F0.imprint","IMPRINT",FACE,{"disambiguationData":[TD([[makeQuery(id+"F0.imprint","IMPRINT",EDGE,{"disambiguationData":[TD([[subQ4,-1.0]])],"derivedFrom":subQ3}),-1.0]])]});}
            var Q30;
            {var subQ1=sQuery(id+"F0.wireOp",EDGE,"E58.trimOffspring");var subQ3=sQuery(id+"F0.wireOp",EDGE,"E25");var subQ5=makeQuery(id+"F0.imprint","INTERSECT",VERTEX,{"derivedFrom":[subQ3,subQ1]});Q30=makeQuery(id+"F0.imprint","IMPRINT",FACE,{"disambiguationData":[TD([[makeQuery(id+"F0.imprint","IMPRINT",EDGE,{"disambiguationData":[TD([[subQ5,1.0]])],"derivedFrom":subQ3}),-1.0]])]});}
            var Q31;
            {var subQ5=sQuery(id+"F0.wireOp",EDGE,"E23.0.startCap");Q31=makeQuery(id+"F0.imprint","IMPRINT",FACE,{"disambiguationData":[TD([[makeQuery(id+"F0.imprint","IMPRINT",EDGE,{"derivedFrom":subQ5}),-1.0]])]});}
            var Q32;
            {var subQ5=sQuery(id+"F0.wireOp",EDGE,"E23.30.startCap");Q32=makeQuery(id+"F0.imprint","IMPRINT",FACE,{"disambiguationData":[TD([[makeQuery(id+"F0.imprint","IMPRINT",EDGE,{"derivedFrom":subQ5}),-1.0]])]});}
            var Q33;
            {var subQ5=sQuery(id+"F0.wireOp",EDGE,"E23.14.startCap");Q33=makeQuery(id+"F0.imprint","IMPRINT",FACE,{"disambiguationData":[TD([[makeQuery(id+"F0.imprint","IMPRINT",EDGE,{"derivedFrom":subQ5}),1.0]])]});}
            var Q34;
            {var subQ1=sQuery(id+"F0.wireOp",EDGE,"E23.25.left");var subQ3=sQuery(id+"F0.wireOp",EDGE,"E25");var subQ5=makeQuery(id+"F0.imprint","INTERSECT",VERTEX,{"derivedFrom":[subQ3,subQ1]});Q34=makeQuery(id+"F0.imprint","IMPRINT",FACE,{"disambiguationData":[TD([[makeQuery(id+"F0.imprint","IMPRINT",EDGE,{"disambiguationData":[TD([[subQ5,-1.0]])],"derivedFrom":subQ3}),-1.0]])]});}
            var Q35;
            {var subQ0=sQuery(id+"F0.wireOp",EDGE,"E23.24.startCap");Q35=makeQuery(id+"F0.imprint","IMPRINT",FACE,{"disambiguationData":[TD([[makeQuery(id+"F0.imprint","IMPRINT",EDGE,{"derivedFrom":subQ0}),-1.0]])]});}
            var Q36;
            {var subQ0=sQuery(id+"F0.wireOp",EDGE,"E23.0.startCap");Q36=makeQuery(id+"F0.imprint","IMPRINT",FACE,{"disambiguationData":[TD([[makeQuery(id+"F0.imprint","IMPRINT",EDGE,{"derivedFrom":subQ0}),1.0]])]});}
            var Q37;
            {var subQ5=sQuery(id+"F0.wireOp",EDGE,"E23.30.startCap");Q37=makeQuery(id+"F0.imprint","IMPRINT",FACE,{"disambiguationData":[TD([[makeQuery(id+"F0.imprint","IMPRINT",EDGE,{"derivedFrom":subQ5}),1.0]])]});}
            var Q38;
            {var subQ2=sQuery(id+"F0.wireOp",EDGE,"E23.3.startCap");Q38=makeQuery(id+"F0.imprint","IMPRINT",FACE,{"disambiguationData":[TD([[makeQuery(id+"F0.imprint","IMPRINT",EDGE,{"derivedFrom":subQ2}),-1.0]])]});}
            var Q39;
            {var subQ0=sQuery(id+"F0.wireOp",EDGE,"E23.21.startCap");Q39=makeQuery(id+"F0.imprint","IMPRINT",FACE,{"disambiguationData":[TD([[makeQuery(id+"F0.imprint","IMPRINT",EDGE,{"derivedFrom":subQ0}),-1.0]])]});}
            var Q40;
            {var subQ3=sQuery(id+"F0.wireOp",EDGE,"E23.14.startCap");Q40=makeQuery(id+"F0.imprint","IMPRINT",FACE,{"disambiguationData":[TD([[makeQuery(id+"F0.imprint","IMPRINT",EDGE,{"derivedFrom":subQ3}),-1.0]])]});}
            var Q41;
            {var subQ5=sQuery(id+"F0.wireOp",EDGE,"E23.25.startCap");Q41=makeQuery(id+"F0.imprint","IMPRINT",FACE,{"disambiguationData":[TD([[makeQuery(id+"F0.imprint","IMPRINT",EDGE,{"derivedFrom":subQ5}),1.0]])]});}
            var Q42;
            {var subQ0=sQuery(id+"F0.wireOp",EDGE,"E23.16.startCap");Q42=makeQuery(id+"F0.imprint","IMPRINT",FACE,{"disambiguationData":[TD([[makeQuery(id+"F0.imprint","IMPRINT",EDGE,{"derivedFrom":subQ0}),-1.0]])]});}
            var Q43;
            {var subQ0=sQuery(id+"F0.wireOp",EDGE,"E23.39.left");var subQ1=sQuery(id+"F0.wireOp",EDGE,"E24");var subQ2=makeQuery(id+"F0.imprint","INTERSECT",VERTEX,{"derivedFrom":[subQ1,subQ0]});Q43=makeQuery(id+"F0.imprint","IMPRINT",FACE,{"disambiguationData":[TD([[makeQuery(id+"F0.imprint","IMPRINT",EDGE,{"disambiguationData":[TD([[subQ2,1.0]])],"derivedFrom":subQ1}),1.0]])]});}
            var Q44;
            {var subQ3=sQuery(id+"F0.wireOp",EDGE,"E23.25.startCap");Q44=makeQuery(id+"F0.imprint","IMPRINT",FACE,{"disambiguationData":[TD([[makeQuery(id+"F0.imprint","IMPRINT",EDGE,{"derivedFrom":subQ3}),-1.0]])]});}
            var Q45;
            {var subQ1=sQuery(id+"F0.wireOp",EDGE,"E23.12.right");var subQ3=sQuery(id+"F0.wireOp",EDGE,"E23.32.right");var subQ5=makeQuery(id+"F0.imprint","INTERSECT",VERTEX,{"derivedFrom":[subQ3,subQ1]});Q45=makeQuery(id+"F0.imprint","IMPRINT",FACE,{"disambiguationData":[TD([[makeQuery(id+"F0.imprint","IMPRINT",EDGE,{"disambiguationData":[TD([[subQ5,-1.0]])],"derivedFrom":subQ3}),-1.0]])]});}
            var Q46;
            {var subQ1=sQuery(id+"F0.wireOp",EDGE,"E25");var subQ5=makeQuery(id+"F0.imprint","INTERSECT",VERTEX,{"derivedFrom":[subQ1,sQuery(id+"F0.wireOp",EDGE,"E23.30.startCap")]});Q46=makeQuery(id+"F0.imprint","IMPRINT",FACE,{"disambiguationData":[TD([[makeQuery(id+"F0.imprint","IMPRINT",EDGE,{"disambiguationData":[TD([[subQ5,1.0]])],"derivedFrom":subQ1}),1.0]])]});}
            var Q47;
            {var subQ0=sQuery(id+"F0.wireOp",EDGE,"E23.17.startCap");Q47=makeQuery(id+"F0.imprint","IMPRINT",FACE,{"disambiguationData":[TD([[makeQuery(id+"F0.imprint","IMPRINT",EDGE,{"derivedFrom":subQ0}),-1.0]])]});}
            var Q48;
            {var subQ0=sQuery(id+"F0.wireOp",EDGE,"E23.0.left");var subQ3=sQuery(id+"F0.wireOp",EDGE,"E25");var subQ4=makeQuery(id+"F0.imprint","INTERSECT",VERTEX,{"derivedFrom":[subQ3,subQ0]});Q48=makeQuery(id+"F0.imprint","IMPRINT",FACE,{"disambiguationData":[TD([[makeQuery(id+"F0.imprint","IMPRINT",EDGE,{"disambiguationData":[TD([[subQ4,-1.0]])],"derivedFrom":subQ3}),-1.0]])]});}
            var Q49;
            {var subQ8=sQuery(id+"F0.wireOp",EDGE,"E23.39.right");Q49=makeQuery(id+"F0.imprint","IMPRINT",FACE,{"disambiguationData":[TD([[makeQuery(id+"F0.imprint","IMPRINT",EDGE,{"derivedFrom":subQ8}),1.0]])]});}
            var Q50;
            {var subQ0=sQuery(id+"F0.wireOp",EDGE,"E23.35.endCap");Q50=makeQuery(id+"F0.imprint","IMPRINT",FACE,{"disambiguationData":[TD([[makeQuery(id+"F0.imprint","IMPRINT",EDGE,{"derivedFrom":subQ0}),-1.0]])]});}
            var Q51;
            {var subQ1=sQuery(id+"F0.wireOp",EDGE,"E25");var subQ5=makeQuery(id+"F0.imprint","INTERSECT",VERTEX,{"derivedFrom":[subQ1,sQuery(id+"F0.wireOp",EDGE,"E23.14.startCap")]});Q51=makeQuery(id+"F0.imprint","IMPRINT",FACE,{"disambiguationData":[TD([[makeQuery(id+"F0.imprint","IMPRINT",EDGE,{"disambiguationData":[TD([[subQ5,1.0]])],"derivedFrom":subQ1}),1.0]])]});}
            var Q52;
            {var subQ0=sQuery(id+"F0.wireOp",EDGE,"E23.11.endCap");Q52=makeQuery(id+"F0.imprint","IMPRINT",FACE,{"disambiguationData":[TD([[makeQuery(id+"F0.imprint","IMPRINT",EDGE,{"derivedFrom":subQ0}),1.0]])]});}
            var Q53;
            {var subQ1=sQuery(id+"F0.wireOp",EDGE,"E25");var subQ5=makeQuery(id+"F0.imprint","INTERSECT",VERTEX,{"derivedFrom":[subQ1,sQuery(id+"F0.wireOp",EDGE,"E23.16.right")]});Q53=makeQuery(id+"F0.imprint","IMPRINT",FACE,{"disambiguationData":[TD([[makeQuery(id+"F0.imprint","IMPRINT",EDGE,{"disambiguationData":[TD([[subQ5,1.0]])],"derivedFrom":subQ1}),1.0]])]});}
            var Q54;
            {var subQ1=sQuery(id+"F0.wireOp",EDGE,"E23.11.right");var subQ3=sQuery(id+"F0.wireOp",EDGE,"E23.3.right");var subQ5=makeQuery(id+"F0.imprint","INTERSECT",VERTEX,{"derivedFrom":[subQ3,subQ1]});Q54=makeQuery(id+"F0.imprint","IMPRINT",FACE,{"disambiguationData":[TD([[makeQuery(id+"F0.imprint","IMPRINT",EDGE,{"disambiguationData":[TD([[subQ5,-1.0]])],"derivedFrom":subQ3}),-1.0]])]});}
            var Q55;
            {var subQ3=sQuery(id+"F0.wireOp",EDGE,"E23.3.startCap");Q55=makeQuery(id+"F0.imprint","IMPRINT",FACE,{"disambiguationData":[TD([[makeQuery(id+"F0.imprint","IMPRINT",EDGE,{"derivedFrom":subQ3}),1.0]])]});}
            var Q56;
            {var subQ1=sQuery(id+"F0.wireOp",EDGE,"E23.14.left");var subQ3=sQuery(id+"F0.wireOp",EDGE,"E25");var subQ5=makeQuery(id+"F0.imprint","INTERSECT",VERTEX,{"derivedFrom":[subQ3,subQ1]});Q56=makeQuery(id+"F0.imprint","IMPRINT",FACE,{"disambiguationData":[TD([[makeQuery(id+"F0.imprint","IMPRINT",EDGE,{"disambiguationData":[TD([[subQ5,-1.0]])],"derivedFrom":subQ3}),-1.0]])]});}
            var Q57;
            {var subQ1=sQuery(id+"F0.wireOp",EDGE,"E25");var subQ5=makeQuery(id+"F0.imprint","INTERSECT",VERTEX,{"derivedFrom":[subQ1,sQuery(id+"F0.wireOp",EDGE,"E23.25.startCap")]});Q57=makeQuery(id+"F0.imprint","IMPRINT",FACE,{"disambiguationData":[TD([[makeQuery(id+"F0.imprint","IMPRINT",EDGE,{"disambiguationData":[TD([[subQ5,1.0]])],"derivedFrom":subQ1}),1.0]])]});}
            var Q58;
            {var subQ1=sQuery(id+"F0.wireOp",EDGE,"E25");var subQ5=makeQuery(id+"F0.imprint","INTERSECT",VERTEX,{"derivedFrom":[subQ1,sQuery(id+"F0.wireOp",EDGE,"E23.0.startCap")]});Q58=makeQuery(id+"F0.imprint","IMPRINT",FACE,{"disambiguationData":[TD([[makeQuery(id+"F0.imprint","IMPRINT",EDGE,{"disambiguationData":[TD([[subQ5,1.0]])],"derivedFrom":subQ1}),1.0]])]});}
            var Q59;
            {var subQ5=sQuery(id+"F0.wireOp",EDGE,"E23.16.startCap");Q59=makeQuery(id+"F0.imprint","IMPRINT",FACE,{"disambiguationData":[TD([[makeQuery(id+"F0.imprint","IMPRINT",EDGE,{"derivedFrom":subQ5}),1.0]])]});}
            var Q60;
            {var subQ1=sQuery(id+"F0.wireOp",EDGE,"E23.16.right");var subQ3=sQuery(id+"F0.wireOp",EDGE,"E25");var subQ5=makeQuery(id+"F0.imprint","INTERSECT",VERTEX,{"derivedFrom":[subQ3,subQ1]});Q60=makeQuery(id+"F0.imprint","IMPRINT",FACE,{"disambiguationData":[TD([[makeQuery(id+"F0.imprint","IMPRINT",EDGE,{"disambiguationData":[TD([[subQ5,1.0]])],"derivedFrom":subQ3}),-1.0]])]});}
            var Q61;
            {var subQ0=sQuery(id+"F0.wireOp",EDGE,"E23.33.right");var subQ3=sQuery(id+"F0.wireOp",EDGE,"E23.21.right");var subQ4=makeQuery(id+"F0.imprint","INTERSECT",VERTEX,{"derivedFrom":[subQ3,subQ0]});Q61=makeQuery(id+"F0.imprint","IMPRINT",FACE,{"disambiguationData":[TD([[makeQuery(id+"F0.imprint","IMPRINT",EDGE,{"disambiguationData":[TD([[subQ4,-1.0]])],"derivedFrom":subQ3}),-1.0]])]});}
            var Q62;
            {var subQ3=sQuery(id+"F0.wireOp",EDGE,"E23.4.startCap");Q62=makeQuery(id+"F0.imprint","IMPRINT",FACE,{"disambiguationData":[TD([[makeQuery(id+"F0.imprint","IMPRINT",EDGE,{"derivedFrom":subQ3}),1.0]])]});}
            var Q63;
            {var subQ1=sQuery(id+"F0.wireOp",EDGE,"E23.4.right");var subQ3=sQuery(id+"F0.wireOp",EDGE,"E23.17.right");var subQ5=makeQuery(id+"F0.imprint","INTERSECT",VERTEX,{"derivedFrom":[subQ3,subQ1]});Q63=makeQuery(id+"F0.imprint","IMPRINT",FACE,{"disambiguationData":[TD([[makeQuery(id+"F0.imprint","IMPRINT",EDGE,{"disambiguationData":[TD([[subQ5,-1.0]])],"derivedFrom":subQ3}),-1.0]])]});}
            var Q64;
            {var subQ0=sQuery(id+"F0.wireOp",EDGE,"E23.11.startCap");Q64=makeQuery(id+"F0.imprint","IMPRINT",FACE,{"disambiguationData":[TD([[makeQuery(id+"F0.imprint","IMPRINT",EDGE,{"derivedFrom":subQ0}),1.0]])]});}
            var Q65;
            {var subQ0=sQuery(id+"F0.wireOp",EDGE,"E23.26.startCap");Q65=makeQuery(id+"F0.imprint","IMPRINT",FACE,{"disambiguationData":[TD([[makeQuery(id+"F0.imprint","IMPRINT",EDGE,{"derivedFrom":subQ0}),1.0]])]});}
            var Q66;
            {var subQ0=sQuery(id+"F0.wireOp",EDGE,"E23.24.startCap");Q66=makeQuery(id+"F0.imprint","IMPRINT",FACE,{"disambiguationData":[TD([[makeQuery(id+"F0.imprint","IMPRINT",EDGE,{"derivedFrom":subQ0}),1.0]])]});}
            var Q67;
            {var subQ0=sQuery(id+"F0.wireOp",EDGE,"E23.40.endCap");Q67=makeQuery(id+"F0.imprint","IMPRINT",FACE,{"disambiguationData":[TD([[makeQuery(id+"F0.imprint","IMPRINT",EDGE,{"derivedFrom":subQ0}),-1.0]])]});}
            var Q68;
            {var subQ0=sQuery(id+"F0.wireOp",EDGE,"E23.21.startCap");Q68=makeQuery(id+"F0.imprint","IMPRINT",FACE,{"disambiguationData":[TD([[makeQuery(id+"F0.imprint","IMPRINT",EDGE,{"derivedFrom":subQ0}),1.0]])]});}
            var Q69;
            {var subQ1=sQuery(id+"F0.wireOp",EDGE,"E23.4.right");var subQ3=sQuery(id+"F0.wireOp",EDGE,"E23.30.right");var subQ5=makeQuery(id+"F0.imprint","INTERSECT",VERTEX,{"derivedFrom":[subQ3,subQ1]});Q69=makeQuery(id+"F0.imprint","IMPRINT",FACE,{"disambiguationData":[TD([[makeQuery(id+"F0.imprint","IMPRINT",EDGE,{"disambiguationData":[TD([[subQ5,1.0]])],"derivedFrom":subQ3}),-1.0]])]});}
            var Q70;
            {var subQ5=sQuery(id+"F0.wireOp",EDGE,"E23.11.startCap");Q70=makeQuery(id+"F0.imprint","IMPRINT",FACE,{"disambiguationData":[TD([[makeQuery(id+"F0.imprint","IMPRINT",EDGE,{"derivedFrom":subQ5}),-1.0]])]});}
            var Q71;
            {var subQ1=sQuery(id+"F0.wireOp",EDGE,"E23.19.left");var subQ3=sQuery(id+"F0.wireOp",EDGE,"E23.24.left");var subQ5=makeQuery(id+"F0.imprint","INTERSECT",VERTEX,{"derivedFrom":[subQ3,subQ1]});Q71=makeQuery(id+"F0.imprint","IMPRINT",FACE,{"disambiguationData":[TD([[makeQuery(id+"F0.imprint","IMPRINT",EDGE,{"disambiguationData":[TD([[subQ5,-1.0]])],"derivedFrom":subQ3}),1.0]])]});}
            var Q72;
            {var subQ8=sQuery(id+"F0.wireOp",EDGE,"E23.42.startCap");Q72=makeQuery(id+"F0.imprint","IMPRINT",FACE,{"disambiguationData":[TD([[makeQuery(id+"F0.imprint","IMPRINT",EDGE,{"derivedFrom":subQ8}),1.0]])]});}
            var Q73;
            {var subQ0=sQuery(id+"F0.wireOp",EDGE,"E23.26.startCap");Q73=makeQuery(id+"F0.imprint","IMPRINT",FACE,{"disambiguationData":[TD([[makeQuery(id+"F0.imprint","IMPRINT",EDGE,{"derivedFrom":subQ0}),-1.0]])]});}
            var Q74;
            {var subQ1=sQuery(id+"F0.wireOp",EDGE,"E23.11.right");var subQ3=sQuery(id+"F0.wireOp",EDGE,"E23.16.right");var subQ5=makeQuery(id+"F0.imprint","INTERSECT",VERTEX,{"derivedFrom":[subQ3,subQ1]});Q74=makeQuery(id+"F0.imprint","IMPRINT",FACE,{"disambiguationData":[TD([[makeQuery(id+"F0.imprint","IMPRINT",EDGE,{"disambiguationData":[TD([[subQ5,1.0]])],"derivedFrom":subQ3}),-1.0]])]});}
            var Q75;
            {var subQ0=sQuery(id+"F0.wireOp",EDGE,"E23.41.right");var subQ1=sQuery(id+"F0.wireOp",EDGE,"E24");var subQ2=makeQuery(id+"F0.imprint","INTERSECT",VERTEX,{"derivedFrom":[subQ1,subQ0]});Q75=makeQuery(id+"F0.imprint","IMPRINT",FACE,{"disambiguationData":[TD([[makeQuery(id+"F0.imprint","IMPRINT",EDGE,{"disambiguationData":[TD([[subQ2,-1.0]])],"derivedFrom":subQ1}),1.0]])]});}
            var Q76;
            {var subQ0=sQuery(id+"F0.wireOp",EDGE,"E23.18.left");var subQ3=sQuery(id+"F0.wireOp",EDGE,"E23.26.left");var subQ4=makeQuery(id+"F0.imprint","INTERSECT",VERTEX,{"derivedFrom":[subQ3,subQ0]});Q76=makeQuery(id+"F0.imprint","IMPRINT",FACE,{"disambiguationData":[TD([[makeQuery(id+"F0.imprint","IMPRINT",EDGE,{"disambiguationData":[TD([[subQ4,-1.0]])],"derivedFrom":subQ3}),1.0]])]});}
            var Q77;
            {var subQ8=sQuery(id+"F0.wireOp",EDGE,"E23.4.startCap");Q77=makeQuery(id+"F0.imprint","IMPRINT",FACE,{"disambiguationData":[TD([[makeQuery(id+"F0.imprint","IMPRINT",EDGE,{"derivedFrom":subQ8}),-1.0]])]});}
            var Q78;
            {var subQ3=sQuery(id+"F0.wireOp",EDGE,"E23.42.endCap");Q78=makeQuery(id+"F0.imprint","IMPRINT",FACE,{"disambiguationData":[TD([[makeQuery(id+"F0.imprint","IMPRINT",EDGE,{"derivedFrom":subQ3}),-1.0]])]});}
            var Q79;
            {var subQ0=sQuery(id+"F0.wireOp",EDGE,"E29");var subQ3=sQuery(id+"F0.wireOp",EDGE,"E25");var subQ4=makeQuery(id+"F0.imprint","INTERSECT",VERTEX,{"disambiguationData":[OD(0.0)],"derivedFrom":[subQ3,subQ0]});Q79=makeQuery(id+"F0.imprint","IMPRINT",FACE,{"disambiguationData":[TD([[makeQuery(id+"F0.imprint","IMPRINT",EDGE,{"disambiguationData":[TD([[subQ4,-1.0]])],"derivedFrom":subQ3}),-1.0]])]});}
            var Q80;
            {var subQ1=sQuery(id+"F0.wireOp",EDGE,"E23.34.left");var subQ3=sQuery(id+"F0.wireOp",EDGE,"E23.25.left");var subQ5=makeQuery(id+"F0.imprint","INTERSECT",VERTEX,{"derivedFrom":[subQ3,subQ1]});Q80=makeQuery(id+"F0.imprint","IMPRINT",FACE,{"disambiguationData":[TD([[makeQuery(id+"F0.imprint","IMPRINT",EDGE,{"disambiguationData":[TD([[subQ5,1.0]])],"derivedFrom":subQ3}),1.0]])]});}
            var Q81;
            {var subQ0=sQuery(id+"F0.wireOp",EDGE,"E23.18.startCap");Q81=makeQuery(id+"F0.imprint","IMPRINT",FACE,{"disambiguationData":[TD([[makeQuery(id+"F0.imprint","IMPRINT",EDGE,{"derivedFrom":subQ0}),1.0]])]});}
            var Q82;
            {var subQ0=sQuery(id+"F0.wireOp",EDGE,"E57.trimOffspring");var subQ3=sQuery(id+"F0.wireOp",EDGE,"E25");var subQ4=makeQuery(id+"F0.imprint","INTERSECT",VERTEX,{"derivedFrom":[subQ3,subQ0]});Q82=makeQuery(id+"F0.imprint","IMPRINT",FACE,{"disambiguationData":[TD([[makeQuery(id+"F0.imprint","IMPRINT",EDGE,{"disambiguationData":[TD([[subQ4,-1.0]])],"derivedFrom":subQ3}),-1.0]])]});}
            var Q83;
            {var subQ0=sQuery(id+"F0.wireOp",EDGE,"E23.34.startCap");Q83=makeQuery(id+"F0.imprint","IMPRINT",FACE,{"disambiguationData":[TD([[makeQuery(id+"F0.imprint","IMPRINT",EDGE,{"derivedFrom":subQ0}),-1.0]])]});}
            var Q84;
            {var subQ1=sQuery(id+"F0.wireOp",EDGE,"E23.29.left");var subQ3=sQuery(id+"F0.wireOp",EDGE,"E23.26.left");var subQ5=makeQuery(id+"F0.imprint","INTERSECT",VERTEX,{"derivedFrom":[subQ3,subQ1]});Q84=makeQuery(id+"F0.imprint","IMPRINT",FACE,{"disambiguationData":[TD([[makeQuery(id+"F0.imprint","IMPRINT",EDGE,{"disambiguationData":[TD([[subQ5,1.0]])],"derivedFrom":subQ3}),1.0]])]});}
            var Q85;
            {var subQ1=sQuery(id+"F0.wireOp",EDGE,"E25");var subQ5=makeQuery(id+"F0.imprint","INTERSECT",VERTEX,{"derivedFrom":[subQ1,sQuery(id+"F0.wireOp",EDGE,"E23.35.startCap")]});Q85=makeQuery(id+"F0.imprint","IMPRINT",FACE,{"disambiguationData":[TD([[makeQuery(id+"F0.imprint","IMPRINT",EDGE,{"disambiguationData":[TD([[subQ5,1.0]])],"derivedFrom":subQ1}),1.0]])]});}
            var Q86;
            {var subQ5=sQuery(id+"F0.wireOp",EDGE,"E23.35.startCap");Q86=makeQuery(id+"F0.imprint","IMPRINT",FACE,{"disambiguationData":[TD([[makeQuery(id+"F0.imprint","IMPRINT",EDGE,{"derivedFrom":subQ5}),-1.0]])]});}
            var Q87;
            {var subQ0=sQuery(id+"F0.wireOp",EDGE,"E25");var subQ1=sQuery(id+"F0.wireOp",EDGE,"E29");var subQ4=makeQuery(id+"F0.imprint","INTERSECT",VERTEX,{"disambiguationData":[OD(0.0)],"derivedFrom":[subQ0,subQ1]});Q87=makeQuery(id+"F0.imprint","IMPRINT",FACE,{"disambiguationData":[TD([[makeQuery(id+"F0.imprint","IMPRINT",EDGE,{"disambiguationData":[TD([[subQ4,-1.0]])],"derivedFrom":subQ0}),1.0]])]});}
            var Q88;
            {var subQ0=sQuery(id+"F0.wireOp",EDGE,"E23.34.startCap");Q88=makeQuery(id+"F0.imprint","IMPRINT",FACE,{"disambiguationData":[TD([[makeQuery(id+"F0.imprint","IMPRINT",EDGE,{"derivedFrom":subQ0}),1.0]])]});}
            var Q89;
            {var subQ0=sQuery(id+"F0.wireOp",EDGE,"E23.18.startCap");Q89=makeQuery(id+"F0.imprint","IMPRINT",FACE,{"disambiguationData":[TD([[makeQuery(id+"F0.imprint","IMPRINT",EDGE,{"derivedFrom":subQ0}),-1.0]])]});}
            var Q90;
            {var subQ2=sQuery(id+"F0.wireOp",EDGE,"E23.40.startCap");Q90=makeQuery(id+"F0.imprint","IMPRINT",FACE,{"disambiguationData":[TD([[makeQuery(id+"F0.imprint","IMPRINT",EDGE,{"derivedFrom":subQ2}),-1.0]])]});}
            var Q91;
            {var subQ0=sQuery(id+"F0.wireOp",EDGE,"E23.35.startCap");Q91=makeQuery(id+"F0.imprint","IMPRINT",FACE,{"disambiguationData":[TD([[makeQuery(id+"F0.imprint","IMPRINT",EDGE,{"derivedFrom":subQ0}),1.0]])]});}
            var Q92;
            {var subQ1=sQuery(id+"F0.wireOp",EDGE,"E23.14.left");var subQ3=sQuery(id+"F0.wireOp",EDGE,"E23.37.left");var subQ5=makeQuery(id+"F0.imprint","INTERSECT",VERTEX,{"derivedFrom":[subQ3,subQ1]});Q92=makeQuery(id+"F0.imprint","IMPRINT",FACE,{"disambiguationData":[TD([[makeQuery(id+"F0.imprint","IMPRINT",EDGE,{"disambiguationData":[TD([[subQ5,-1.0]])],"derivedFrom":subQ3}),1.0]])]});}
            var Q93;
            {var subQ0=sQuery(id+"F0.wireOp",EDGE,"E23.26.endCap");Q93=makeQuery(id+"F0.imprint","IMPRINT",FACE,{"disambiguationData":[TD([[makeQuery(id+"F0.imprint","IMPRINT",EDGE,{"derivedFrom":subQ0}),1.0]])]});}
            var Q94;
            {var subQ0=sQuery(id+"F0.wireOp",EDGE,"E23.32.startCap");Q94=makeQuery(id+"F0.imprint","IMPRINT",FACE,{"disambiguationData":[TD([[makeQuery(id+"F0.imprint","IMPRINT",EDGE,{"derivedFrom":subQ0}),-1.0]])]});}
            var Q95;
            {var subQ3=sQuery(id+"F0.wireOp",EDGE,"E23.35.endCap");Q95=makeQuery(id+"F0.imprint","IMPRINT",FACE,{"disambiguationData":[TD([[makeQuery(id+"F0.imprint","IMPRINT",EDGE,{"derivedFrom":subQ3}),1.0]])]});}
            var Q96;
            {var subQ1=sQuery(id+"F0.wireOp",EDGE,"E23.12.right");var subQ3=sQuery(id+"F0.wireOp",EDGE,"E23.35.right");var subQ5=makeQuery(id+"F0.imprint","INTERSECT",VERTEX,{"derivedFrom":[subQ3,subQ1]});Q96=makeQuery(id+"F0.imprint","IMPRINT",FACE,{"disambiguationData":[TD([[makeQuery(id+"F0.imprint","IMPRINT",EDGE,{"disambiguationData":[TD([[subQ5,1.0]])],"derivedFrom":subQ3}),-1.0]])]});}
            var Q97;
            {var subQ5=sQuery(id+"F0.wireOp",EDGE,"E23.19.startCap");Q97=makeQuery(id+"F0.imprint","IMPRINT",FACE,{"disambiguationData":[TD([[makeQuery(id+"F0.imprint","IMPRINT",EDGE,{"derivedFrom":subQ5}),1.0]])]});}
            var Q98;
            {var subQ8=sQuery(id+"F0.wireOp",EDGE,"E23.33.startCap");Q98=makeQuery(id+"F0.imprint","IMPRINT",FACE,{"disambiguationData":[TD([[makeQuery(id+"F0.imprint","IMPRINT",EDGE,{"derivedFrom":subQ8}),-1.0]])]});}
            var Q99;
            {var subQ0=sQuery(id+"F0.wireOp",EDGE,"E23.19.startCap");Q99=makeQuery(id+"F0.imprint","IMPRINT",FACE,{"disambiguationData":[TD([[makeQuery(id+"F0.imprint","IMPRINT",EDGE,{"derivedFrom":subQ0}),-1.0]])]});}
            var Q100;
            {var subQ5=sQuery(id+"F0.wireOp",EDGE,"E23.14.endCap");Q100=makeQuery(id+"F0.imprint","IMPRINT",FACE,{"disambiguationData":[TD([[makeQuery(id+"F0.imprint","IMPRINT",EDGE,{"derivedFrom":subQ5}),1.0]])]});}
            var Q101;
            {var subQ0=sQuery(id+"F0.wireOp",EDGE,"E23.17.startCap");Q101=makeQuery(id+"F0.imprint","IMPRINT",FACE,{"disambiguationData":[TD([[makeQuery(id+"F0.imprint","IMPRINT",EDGE,{"derivedFrom":subQ0}),1.0]])]});}
            var Q102;
            {var subQ0=sQuery(id+"F0.wireOp",EDGE,"E23.14.endCap");Q102=makeQuery(id+"F0.imprint","IMPRINT",FACE,{"disambiguationData":[TD([[makeQuery(id+"F0.imprint","IMPRINT",EDGE,{"derivedFrom":subQ0}),-1.0]])]});}
            var Q103;
            {var subQ5=sQuery(id+"F0.wireOp",EDGE,"E23.32.startCap");Q103=makeQuery(id+"F0.imprint","IMPRINT",FACE,{"disambiguationData":[TD([[makeQuery(id+"F0.imprint","IMPRINT",EDGE,{"derivedFrom":subQ5}),1.0]])]});}
            var Q104;
            {var subQ0=sQuery(id+"F0.wireOp",EDGE,"E23.26.endCap");Q104=makeQuery(id+"F0.imprint","IMPRINT",FACE,{"disambiguationData":[TD([[makeQuery(id+"F0.imprint","IMPRINT",EDGE,{"derivedFrom":subQ0}),-1.0]])]});}
            var Q105;
            {var subQ0=sQuery(id+"F0.wireOp",EDGE,"E23.33.startCap");Q105=makeQuery(id+"F0.imprint","IMPRINT",FACE,{"disambiguationData":[TD([[makeQuery(id+"F0.imprint","IMPRINT",EDGE,{"derivedFrom":subQ0}),1.0]])]});}
            var Q106;
            {var subQ1=sQuery(id+"F0.wireOp",EDGE,"E23.33.right");var subQ3=sQuery(id+"F0.wireOp",EDGE,"E23.0.right");var subQ5=makeQuery(id+"F0.imprint","INTERSECT",VERTEX,{"derivedFrom":[subQ3,subQ1]});Q106=makeQuery(id+"F0.imprint","IMPRINT",FACE,{"disambiguationData":[TD([[makeQuery(id+"F0.imprint","IMPRINT",EDGE,{"disambiguationData":[TD([[subQ5,1.0]])],"derivedFrom":subQ3}),-1.0]])]});}
            var Q107;
            {var subQ6=sQuery(id+"F0.wireOp",EDGE,"E23.42.startCap");Q107=makeQuery(id+"F0.imprint","IMPRINT",FACE,{"disambiguationData":[TD([[makeQuery(id+"F0.imprint","IMPRINT",EDGE,{"derivedFrom":subQ6}),-1.0]])]});}
            var Q108;
            {var subQ0=sQuery(id+"F0.wireOp",EDGE,"E59.trimOffspring");var subQ3=sQuery(id+"F0.wireOp",EDGE,"E23.19.left");var subQ4=makeQuery(id+"F0.imprint","INTERSECT",VERTEX,{"derivedFrom":[subQ3,subQ0]});Q108=makeQuery(id+"F0.imprint","IMPRINT",FACE,{"disambiguationData":[TD([[makeQuery(id+"F0.imprint","IMPRINT",EDGE,{"disambiguationData":[TD([[subQ4,-1.0]])],"derivedFrom":subQ3}),1.0]])]});}
            var Q109;
            {var subQ0=sQuery(id+"F0.wireOp",EDGE,"E23.34.endCap");Q109=makeQuery(id+"F0.imprint","IMPRINT",FACE,{"disambiguationData":[TD([[makeQuery(id+"F0.imprint","IMPRINT",EDGE,{"derivedFrom":subQ0}),-1.0]])]});}
            var Q110;
            {var subQ5=sQuery(id+"F0.wireOp",EDGE,"E23.27.startCap");Q110=makeQuery(id+"F0.imprint","IMPRINT",FACE,{"disambiguationData":[TD([[makeQuery(id+"F0.imprint","IMPRINT",EDGE,{"derivedFrom":subQ5}),-1.0]])]});}
            var Q111;
            {var subQ0=sQuery(id+"F0.wireOp",EDGE,"E23.34.endCap");Q111=makeQuery(id+"F0.imprint","IMPRINT",FACE,{"disambiguationData":[TD([[makeQuery(id+"F0.imprint","IMPRINT",EDGE,{"derivedFrom":subQ0}),1.0]])]});}
            var Q112;
            {var subQ1=sQuery(id+"F0.wireOp",EDGE,"E23.1.left");var subQ3=sQuery(id+"F0.wireOp",EDGE,"E23.34.left");var subQ5=makeQuery(id+"F0.imprint","INTERSECT",VERTEX,{"derivedFrom":[subQ3,subQ1]});Q112=makeQuery(id+"F0.imprint","IMPRINT",FACE,{"disambiguationData":[TD([[makeQuery(id+"F0.imprint","IMPRINT",EDGE,{"disambiguationData":[TD([[subQ5,1.0]])],"derivedFrom":subQ3}),1.0]])]});}
            var Q113;
            {var subQ1=sQuery(id+"F0.wireOp",EDGE,"E23.27.left");var subQ3=sQuery(id+"F0.wireOp",EDGE,"E23.37.left");var subQ5=makeQuery(id+"F0.imprint","INTERSECT",VERTEX,{"derivedFrom":[subQ3,subQ1]});Q113=makeQuery(id+"F0.imprint","IMPRINT",FACE,{"disambiguationData":[TD([[makeQuery(id+"F0.imprint","IMPRINT",EDGE,{"disambiguationData":[TD([[subQ5,1.0]])],"derivedFrom":subQ3}),1.0]])]});}
            var Q114;
            {var subQ0=sQuery(id+"F0.wireOp",EDGE,"E23.27.startCap");Q114=makeQuery(id+"F0.imprint","IMPRINT",FACE,{"disambiguationData":[TD([[makeQuery(id+"F0.imprint","IMPRINT",EDGE,{"derivedFrom":subQ0}),1.0]])]});}
            var Q115;
            Q115=makeQuery(id+"F0.imprint","IMPRINT",FACE,{"disambiguationData":[TD([[makeQuery(id+"F0.imprint","IMPRINT",EDGE,{"derivedFrom":sQuery(id+"F0.wireOp",EDGE,"E1.5.right")}),1.0]])]});
            extrude(context, id + "F1", {"entities" : qUnion([Q0, Q1, Q2, Q3, Q4, Q5, Q6, Q7, Q8, Q9, Q10, Q11, Q12, Q13, Q14, Q15, Q16, Q17, Q18, Q19, Q20, Q21, Q22, Q23, Q24, Q25, Q26, Q27, Q28, Q29, Q30, Q31, Q32, Q33, Q34, Q35, Q36, Q37, Q38, Q39, Q40, Q41, Q42, Q43, Q44, Q45, Q46, Q47, Q48, Q49, Q50, Q51, Q52, Q53, Q54, Q55, Q56, Q57, Q58, Q59, Q60, Q61, Q62, Q63, Q64, Q65, Q66, Q67, Q68, Q69, Q70, Q71, Q72, Q73, Q74, Q75, Q76, Q77, Q78, Q79, Q80, Q81, Q82, Q83, Q84, Q85, Q86, Q87, Q88, Q89, Q90, Q91, Q92, Q93, Q94, Q95, Q96, Q97, Q98, Q99, Q100, Q101, Q102, Q103, Q104, Q105, Q106, Q107, Q108, Q109, Q110, Q111, Q112, Q113, Q114, Q115]), "depth" : .4 * mm});
        }
    });
